# Revit family: Gira_0211135
name_source: partatom
category: Electrical Fixtures
revit_build: Autodesk Revit 2017 (Build: 20160225_1515(x64)
units: mm (PartAtom-declared; Revit-internal decimal feet)

## family parameters
Cut with Voids When Loaded = No
Host = Face
Maintain Annotation Orientation = No
Part Type = Normal
Room Calculation Point = No
Round Connector Dimension = Use Diameter
Shared = No

## types (1)
- Abdeckrahmen 1f Gira Studio G Schwarz
    Anzahl der Einheiten = 1
    Anzahl der Einheiten horizontal = 1
    Anzahl der Einheiten vertikal = 1
    Ausführung der Oberfläche = glänzend
    Available = Yes
    BIM (1) = https://media.live.bim.site
    BIM (2) = https://media.live.bim.site
    Befestigungsart = Klemmbefestigung
    Category = Abdeckrahmen
    Data sheet (1) = https://katalog.gira.de
    Default Elevation = 1219 mm
    Description = Abdeckrahmen Gira Studio Glas Schwarz 1fach Installation in handelsübliche Gerätedosen, beliebig erweiterbar durch Installation in Gerätedosen mit Abstandsstutzen. Für die Aufputz-Installation: Gira Studio, Gehäuse 1fach mit Abdeckrahmen 1fach, beliebig erweiterbar.
    Farbe = schwarz
    GTIN = 4010337045656
    Geeignet für Einbauinstallation = Nein
    Geeignet für Geräteeinbaukanal = Nein
    Geeignet für Unterflurkanaldose = Nein
    Geeignet für Unterputz-Installation = Ja
    HAN = 0211135
    Halogenfrei = Nein
    HeinzeBIM = https://bimportal.heinze.de
    Kategorie = Abdeckrahmen
    Keynote = Studio_Rahmen_Abdeckplatte_1fach
    Manufacturer = Gira
    Manufacturer URL = https://www.gira.de
    Mit Klappdeckel = Nein
    Mit Montagerahmen = Nein
    Montagerichtung = horizontal und vertikal
    Name = Abdeckrahmen 1f Gira Studio G Schwarz
    Oberfläche = sonstige
    Region = DE
    Schutzart (IP) = IP20
    Textfeld/Beschriftungsfläche = Nein
    Transparent = Nein
    URL = http://katalog.gira.de
    Verfügbar = Ja
    Werkstoff = Glas
    Werkstoffgüte = Echtglas

## geometry (parser evidence)
native form markers: Blend x2, Sweep x3
no freeform markers — native parametric forms only
